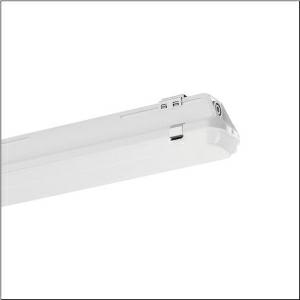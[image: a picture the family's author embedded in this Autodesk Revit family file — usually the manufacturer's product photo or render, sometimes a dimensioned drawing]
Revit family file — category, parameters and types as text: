
# Revit family: monsun_11_51fp207p4b0u
name_source: partatom
category: Lighting Fixtures
units: mm (PartAtom-declared; Revit-internal decimal feet)

## family parameters
Cut with Voids When Loaded = No
Host = Face
Light Source = No
Part Type = Normal
Room Calculation Point = No
Round Connector Dimension = Use Diameter
Shared = No

## types (1)
- Monsun 11 (1 x LED, 10910 lm, 62.4 W, 4000K)
    Apparent Load = 62 VA
    CIE Flux Codes = 45 75 93 94 100
    Color Rendering = 80
    Color Temperature = 4000K
    Default Elevation = 1800 mm
    Description = Monsun 11, damp-proof luminaire, chain hanger, primary optical cover: enclosure, of PC, light emission: direct distribution, primary light characteristic: symmetric, installation type: suspended mounting, surface-mounted, horizontal mounting, vertical mounting, LED, rated luminous flux: 10.910lm, luminous efficacy: 175lm/W, light colour: 840, colour temperature: 4000K, control gear: ON/OFF, with terminal, 3-pole, max. 2.5mm², mains connection: 220..240V, AC, 50/60Hz, rated input power: 62W, luminaire housing, of glass-fibre reinforced polyester, uncoated, bright grey, incl. chain hanger, length: 1.590mm, width: 90mm, height: 88mm, clip for enclosure, of stainless steel (V2A), ceiling mounting element, of stainless steel (V2A), chain hanger, of stainless steel (V2A), protection rating (complete): IP66, insulation class (complete): insulation class I (protective earthing), certification: CE, ENEC, VDE, UKCA, protection symbol: D, impact resistance: IK08, permissible operating ambient temperature: -35..+35°C, standard: EN 50419, EN 60598-2-1, contact your sales advisor before using the luminaires in applications with unclear chemical exposure, large temperature fluctuations or condensation-forming humidity, LABS conformity tested according to VDMA 24364:2018-05, no direct snow, no direct sun, no direct rain, for indoor or canopied outdoor use, corresponds to IFS (International Featured Standards) requirements for safety and quality in the food industry, packaging unit: 1 piece
    Height = 89 mm
    Lamp = 1 x LED
    Lamp Light Flux = 10910 lm
    Lamp Power = 62.4 W
    Lamp count = 1
    Length = 1590 mm
    Luminous efficacy = 175 lm/W
    Manufacturer = Siteco
    ModVariant = No
    Model = 51FP207P4B0U
    Mounting Place = Ceiling
    Mounting Type = Surface mounted
    Number of Poles = 1
    OnlyDefault = Yes
    Power Factor = 1
    Product Name = Monsun 11
    Product group = damp-proof luminaire
    ProductGroupID = 300
    Protection Class = Protection class I
    Protection Degree = IP 66
    RLX_Detail_Level = 1
    RLX_Emergency_Light_Flux = 0 lm
    RLX_Emergency_Type = 0
    RLX_Emergency_Type_DB = No
    RlxData = <blob elided: 88349 chars, md5=356ea08e>
    Socket = socket
    Standby Power = 0 W
    System Light Flux = 10910 lm
    System Power = 62 W
    Type Comments = Product without accessories
    Type Image = l_1349237.jpg
    URL = http://relux.com
    VarID = ---
    Voltage = 0 V
    Weight = 0.00 kg
    Width = 90 mm

## geometry (parser evidence)
native form markers: Blend x4, Sweep x13
no freeform markers — native parametric forms only
